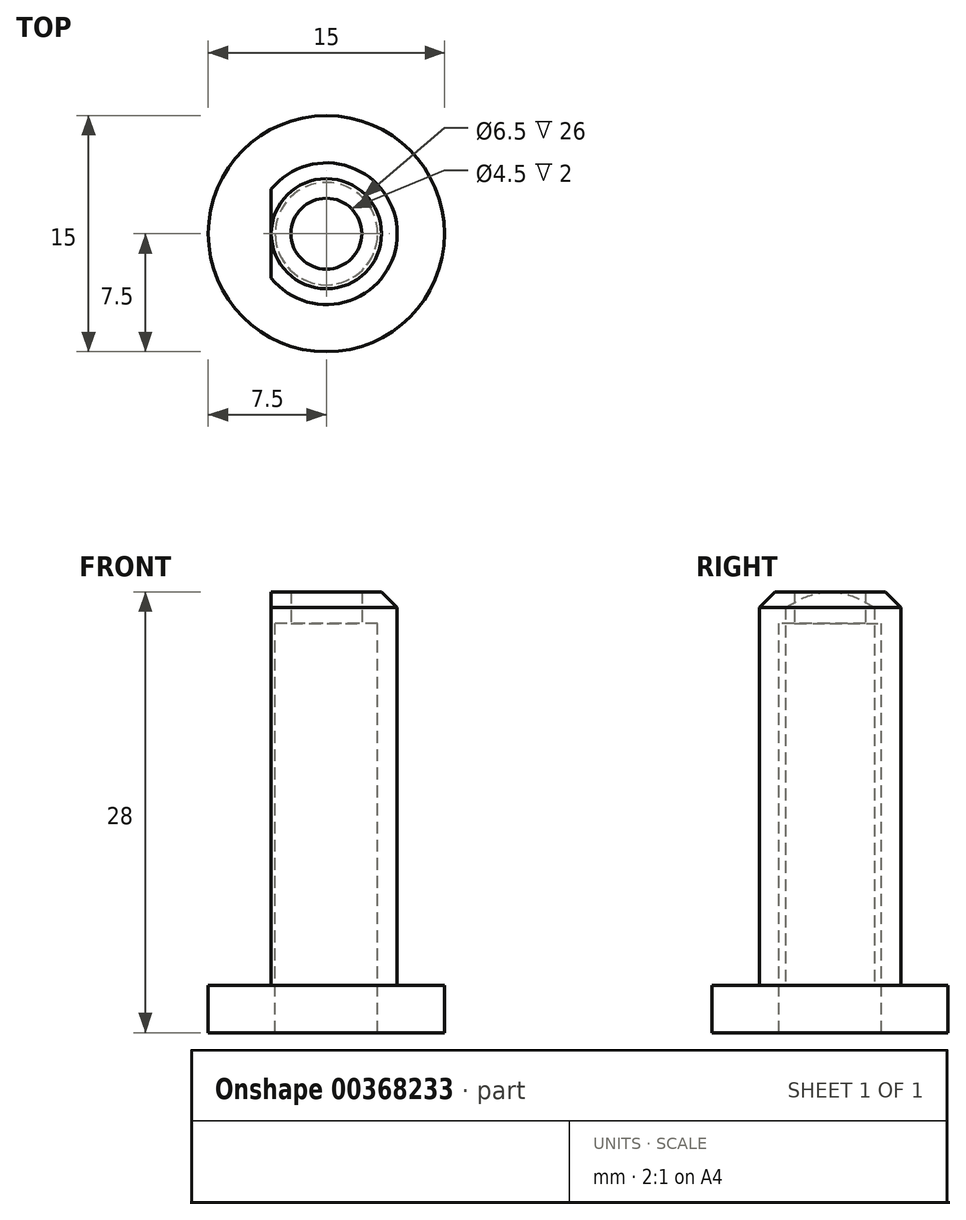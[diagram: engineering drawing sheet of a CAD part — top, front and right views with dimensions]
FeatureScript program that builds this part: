
annotation { "Feature Type Name" : "Feature", "Feature Type Description" : "" }
export const myFeature = defineFeature(function(context is Context, id is Id, definition is map)
    precondition{}
    {
        {
            var Q0;
            Q0=qCreatedBy(makeId("Top.planeOp"),FACE);
            var sketch = newSketch(context, id + "F0", { "sketchPlane" : qUnion([Q0])});
            skCircle(sketch, "E0", {"center": v(0, 0) * mm, "radius": 7.5 * mm});
            skArc(sketch, "E1", {"start": v(-3.5, -2.83) * mm, "mid": v(4.5, 0) * mm, "end": v(-3.5, 2.83) * mm});
            skLineSegment(sketch, "E2", {"start": v(-3.5, 2.83) * mm, "end": v(-3.5, -2.83) * mm});
            skSolve(sketch);
        }
        {
            var Q0;
            Q0=makeQuery(id+"F0.imprint","IMPRINT",FACE,{"disambiguationData":[TD([[makeQuery(id+"F0.imprint","IMPRINT",EDGE,{"derivedFrom":sQuery(id+"F0.wireOp",EDGE,"E1")}),1.0]])]});
            extrude(context, id + "F1", {"entities" : qUnion([Q0]), "depth" : 25 * mm});
        }
        {
            var Q0;
            Q0=makeQuery(id+"F0.imprint","IMPRINT",FACE,{"disambiguationData":[TD([[makeQuery(id+"F0.imprint","IMPRINT",EDGE,{"derivedFrom":sQuery(id+"F0.wireOp",EDGE,"E1")}),1.0]])]});
            var Q1;
            Q1=makeQuery(id+"F0.imprint","IMPRINT",FACE,{"disambiguationData":[TD([[makeQuery(id+"F0.imprint","IMPRINT",EDGE,{"derivedFrom":sQuery(id+"F0.wireOp",EDGE,"E0")}),1.0]])]});
            extrude(context, id + "F2", {"entities" : qUnion([Q0, Q1]), "operationType" : NewBodyOperationType.ADD, "oppositeDirection" : true, "depth" : 3 * mm});
        }
        {
            var Q0;
            Q0=sQuery(id+"F0.wireOp",VERTEX,"E1.center");
            var Q1;
            Q1=makeQuery(id+"F1.opExtrude","SWEPT_BODY",BODY,{"disambiguationData":[OSD([sQuery(id+"F0.wireOp",EDGE,"E1"),sQuery(id+"F0.wireOp",EDGE,"E2")])]});
            hole(context, id + "F3", {"style" : HoleStyle.SIMPLE, "endStyle" : HoleEndStyle.THROUGH, "holeDiameter" : 6.5 * mm, "isTappedThrough" : true, "tappedDepth" : 12 * mm, "tapClearance" : 3, "locations" : qUnion([Q0]), "scope" : qUnion([Q1])});
        }
        {
            var Q0;
            Q0=sQuery(id+"F0.wireOp",VERTEX,"E1.center");
            var Q1;
            Q1=makeQuery(id+"F1.opExtrude","SWEPT_BODY",BODY,{"disambiguationData":[OSD([sQuery(id+"F0.wireOp",EDGE,"E1"),sQuery(id+"F0.wireOp",EDGE,"E2")])]});
            hole(context, id + "F4", {"style" : HoleStyle.C_BORE, "endStyle" : HoleEndStyle.BLIND, "oppositeDirection" : true, "holeDiameter" : 4.5 * mm, "cBoreDiameter" : 6.5 * mm, "cBoreDepth" : 23 * mm, "holeDepth" : 25 * mm, "isTappedThrough" : true, "tappedDepth" : 12 * mm, "tapClearance" : 3, "startFromSketch" : true, "locations" : qUnion([Q0]), "scope" : qUnion([Q1])});
        }
        {
            var Q0;
            Q0=makeQuery(id+"F1.opExtrude","CAP_EDGE",EDGE,{"disambiguationData":[OSD([sQuery(id+"F0.wireOp",EDGE,"E1")])],"isStart":false});
            var Q1;
            Q1=makeQuery(id+"F4.hole-0.boolean.opBoolean","COPY",EDGE,{"derivedFrom":makeQuery(id+"F4.hole-0.opRevolve","SWEPT_EDGE",EDGE,{"disambiguationData":[OSD([sQuery(id+"F4.hole-0.sketch.wireOp",EDGE,"cbore_start_line_1"),sQuery(id+"F4.hole-0.sketch.wireOp",EDGE,"core_line_2")])]})});
            chamfer(context, id + "F5", {"entities" : qUnion([Q0, Q1]), "width" : 1 * mm, "tangentPropagation" : true});
        }
    });
